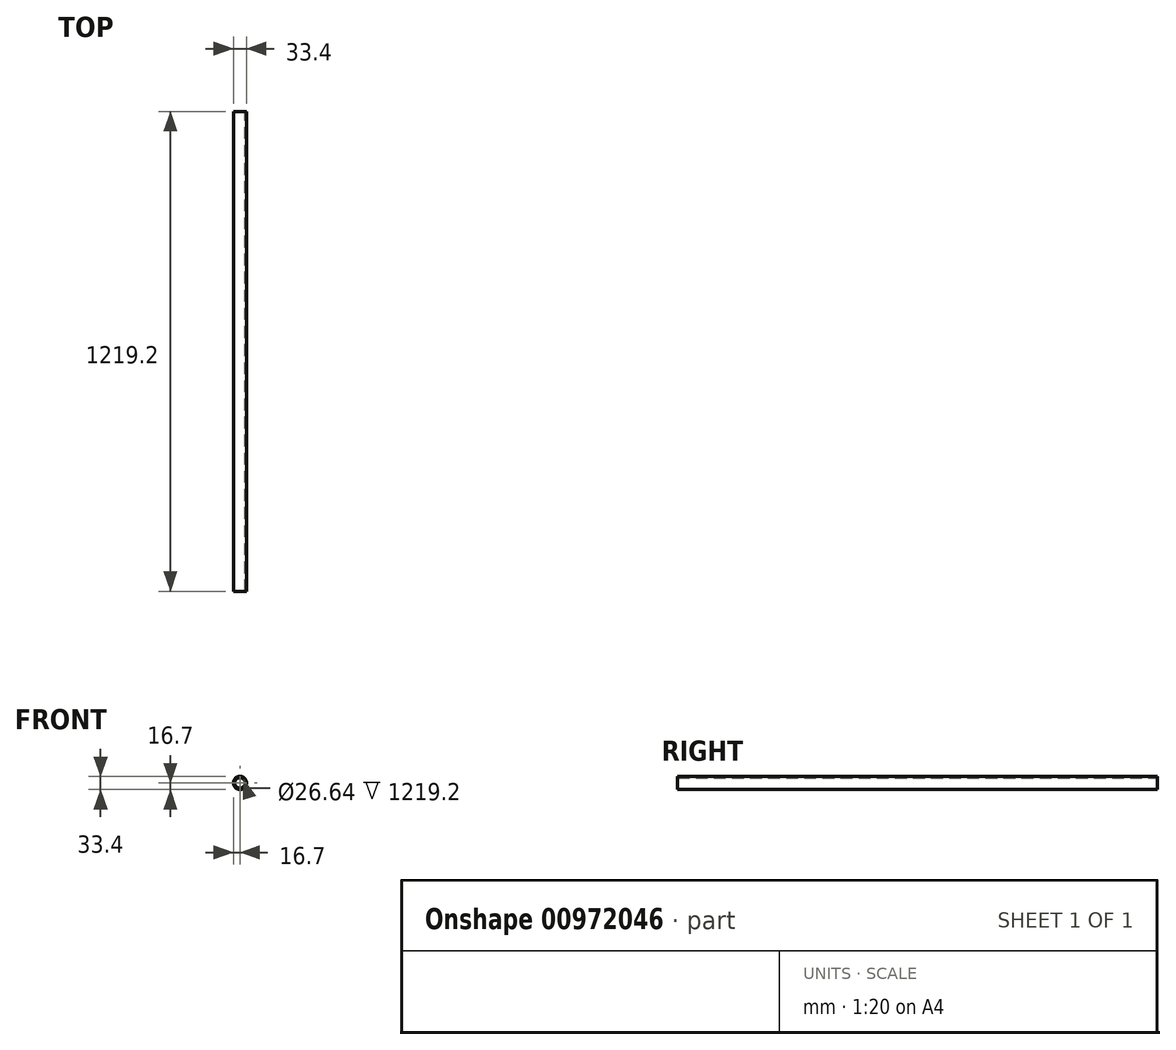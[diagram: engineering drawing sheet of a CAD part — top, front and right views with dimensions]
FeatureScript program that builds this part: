
annotation { "Feature Type Name" : "Feature", "Feature Type Description" : "" }
export const myFeature = defineFeature(function(context is Context, id is Id, definition is map)
    precondition{}
    {
        {
            var Q0;
            Q0=qCreatedBy(makeId("Front.planeOp"),FACE);
            var sketch = newSketch(context, id + "F0", { "sketchPlane" : qUnion([Q0])});
            skCircle(sketch, "E0", {"center": v(0, 0) * mm, "radius": 16.7 * mm});
            skCircle(sketch, "E1", {"center": v(0, 0) * mm, "radius": 13.32 * mm});
            skSolve(sketch);
        }
        {
            var Q0;
            Q0=makeQuery(id+"F0.imprint","IMPRINT",FACE,{"disambiguationData":[TD([[makeQuery(id+"F0.imprint","IMPRINT",EDGE,{"derivedFrom":sQuery(id+"F0.wireOp",EDGE,"E0")}),1.0]])]});
            extrude(context, id + "F1", {"entities" : qUnion([Q0]), "depth" : 1219.2 * mm, "offsetDistance" : 25.4 * mm});
        }
    });
